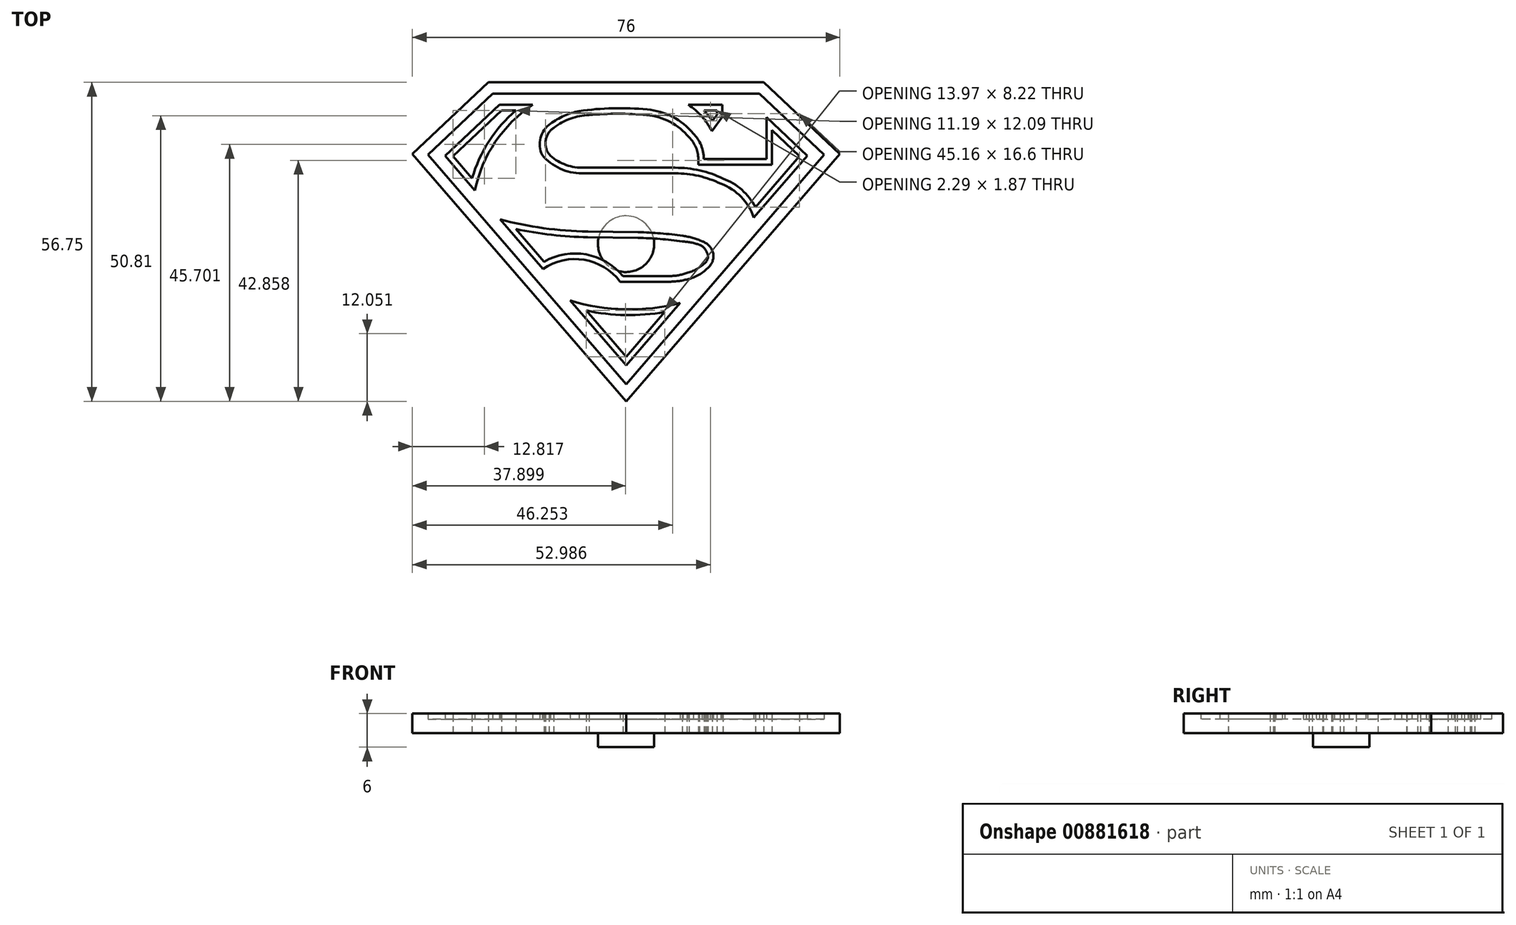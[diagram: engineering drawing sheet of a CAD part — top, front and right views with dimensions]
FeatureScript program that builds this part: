
annotation { "Feature Type Name" : "Feature", "Feature Type Description" : "" }
export const myFeature = defineFeature(function(context is Context, id is Id, definition is map)
    precondition{}
    {
        {
            var Q0;
            Q0=qCreatedBy(makeId("Top.planeOp"),FACE);
            var sketch = newSketch(context, id + "F0", { "sketchPlane" : qUnion([Q0])});
            skLineSegment(sketch, "E0", {"start": v(-24.5, 28.75) * mm, "end": v(24.5, 28.75) * mm});
            skLineSegment(sketch, "E1", {"start": v(24.5, 28.75) * mm, "end": v(38, 16) * mm});
            skLineSegment(sketch, "E2", {"start": v(38, 16) * mm, "end": v(0, -28) * mm});
            skLineSegment(sketch, "E3", {"start": v(0, -28) * mm, "end": v(-38, 16) * mm});
            skLineSegment(sketch, "E4", {"start": v(-38, 16) * mm, "end": v(-24.5, 28.75) * mm});
            skSolve(sketch);
        }
        {
            var Q0;
            Q0 = qSketchRegion(id + "F0", true);
            extrude(context, id + "F1", {"entities" : qUnion([Q0]), "depth" : 2.5 * mm, "offsetDistance" : 25 * mm});
        }
        {
            var Q0;
            Q0=makeQuery(id+"F1.opExtrude","CAP_FACE",FACE,{"disambiguationData":[OSD([sQuery(id+"F0.wireOp",EDGE,"E0"),sQuery(id+"F0.wireOp",EDGE,"E1"),sQuery(id+"F0.wireOp",EDGE,"E2"),sQuery(id+"F0.wireOp",EDGE,"E3"),sQuery(id+"F0.wireOp",EDGE,"E4")])],"isStart":false});
            var sketch = newSketch(context, id + "F2", { "sketchPlane" : qUnion([Q0])});
            skLineSegment(sketch, "E5", {"start": v(-38, 16) * mm, "end": v(-24.5, 28.75) * mm});
            skLineSegment(sketch, "E6", {"start": v(-24.5, 28.75) * mm, "end": v(24.5, 28.75) * mm});
            skLineSegment(sketch, "E7", {"start": v(24.5, 28.75) * mm, "end": v(38, 16) * mm});
            skLineSegment(sketch, "E8", {"start": v(38, 16) * mm, "end": v(0, -28) * mm});
            skLineSegment(sketch, "E9", {"start": v(0, -28) * mm, "end": v(-38, 16) * mm});
            skLineSegment(sketch, "E10.0", {"start": v(-35.24, 15.86) * mm, "end": v(0, -24.94) * mm});
            skLineSegment(sketch, "E10.1", {"start": v(-23.7, 26.75) * mm, "end": v(-35.24, 15.86) * mm});
            skLineSegment(sketch, "E10.2", {"start": v(0, -24.94) * mm, "end": v(35.24, 15.86) * mm});
            skLineSegment(sketch, "E10.3", {"start": v(35.24, 15.86) * mm, "end": v(23.7, 26.75) * mm});
            skLineSegment(sketch, "E10.4", {"start": v(23.7, 26.75) * mm, "end": v(-23.7, 26.75) * mm});
            skLineSegment(sketch, "E11", {"start": v(-32.16, 15.66) * mm, "end": v(-22.54, 24.75) * mm});
            skLineSegment(sketch, "E12", {"start": v(-22.54, 24.75) * mm, "end": v(-16.62, 24.75) * mm});
            skLineSegment(sketch, "E13", {"start": v(-32.16, 15.66) * mm, "end": v(-26.87, 9.54) * mm});
            skLineSegment(sketch, "E14", {"start": v(32.21, 15.7) * mm, "end": v(22.71, 4.7) * mm});
            skLineSegment(sketch, "E15", {"start": v(32.21, 15.7) * mm, "end": v(24.97, 22.54) * mm});
            skLineSegment(sketch, "E16", {"start": v(-22.39, 4.35) * mm, "end": v(-14.78, -4.46) * mm});
            skLineSegment(sketch, "E17", {"start": v(-9.95, -10.06) * mm, "end": v(0.01, -21.59) * mm});
            skLineSegment(sketch, "E18", {"start": v(9.6, -10.48) * mm, "end": v(0.01, -21.59) * mm});
            skLineSegment(sketch, "E19", {"start": v(11.1, 24.75) * mm, "end": v(17.13, 24.75) * mm});
            skArc(sketch, "E20", {"start": v(-16.62, 24.75) * mm, "mid": v(-23.24, 18.15) * mm, "end": v(-26.87, 9.54) * mm});
            skArc(sketch, "E21", {"start": v(15.26, 20.07) * mm, "mid": v(13.48, 22.67) * mm, "end": v(11.1, 24.75) * mm});
            skLineSegment(sketch, "E22", {"start": v(17.13, 24.75) * mm, "end": v(17.13, 22.58) * mm});
            skLineSegment(sketch, "E23", {"start": v(17.13, 22.58) * mm, "end": v(15.26, 20.07) * mm});
            skLineSegment(sketch, "E24", {"start": v(24.97, 22.54) * mm, "end": v(24.97, 15.1) * mm});
            skLineSegment(sketch, "E25", {"start": v(-7.86, 12.56) * mm, "end": v(8.75, 12.56) * mm});
            skArc(sketch, "E26", {"start": v(22.71, 4.7) * mm, "mid": v(20.46, 8.36) * mm, "end": v(16.86, 10.72) * mm});
            skArc(sketch, "E27", {"start": v(16.86, 10.72) * mm, "mid": v(12.9, 12.1) * mm, "end": v(8.75, 12.56) * mm});
            skLineSegment(sketch, "E28", {"start": v(-1.06, -6.7) * mm, "end": v(7.73, -6.7) * mm});
            skArc(sketch, "E29", {"start": v(-1.06, -6.7) * mm, "mid": v(-7.47, -2.82) * mm, "end": v(-14.78, -4.46) * mm});
            skArc(sketch, "E30", {"start": v(-22.39, 4.35) * mm, "mid": v(-14.66, 2.8) * mm, "end": v(-6.8, 2.21) * mm});
            skLineSegment(sketch, "E31", {"start": v(-6.8, 2.21) * mm, "end": v(2.13, 2.08) * mm});
            skArc(sketch, "E32", {"start": v(10.13, 1.43) * mm, "mid": v(6.14, 1.89) * mm, "end": v(2.13, 2.08) * mm});
            skArc(sketch, "E33", {"start": v(-9.95, -10.06) * mm, "mid": v(-0.2, -11.64) * mm, "end": v(9.6, -10.48) * mm});
            skLineSegment(sketch, "E34.0", {"start": v(-30.78, 15.6) * mm, "end": v(-22.14, 23.75) * mm});
            skLineSegment(sketch, "E35.0", {"start": v(-30.78, 15.6) * mm, "end": v(-27.38, 11.65) * mm});
            skLineSegment(sketch, "E36.0", {"start": v(-22.14, 23.75) * mm, "end": v(-19.6, 23.75) * mm});
            skArc(sketch, "E37.0", {"start": v(-19.6, 23.75) * mm, "mid": v(-24.37, 18.27) * mm, "end": v(-27.38, 11.65) * mm});
            skArc(sketch, "E38.0", {"start": v(15.36, 21.87) * mm, "mid": v(14.64, 22.84) * mm, "end": v(13.84, 23.75) * mm});
            skLineSegment(sketch, "E39.0", {"start": v(13.84, 23.75) * mm, "end": v(16.13, 23.75) * mm});
            skLineSegment(sketch, "E40.0", {"start": v(16.13, 23.75) * mm, "end": v(16.13, 22.9) * mm});
            skLineSegment(sketch, "E41.0", {"start": v(16.13, 22.9) * mm, "end": v(15.36, 21.87) * mm});
            skLineSegment(sketch, "E42.0", {"start": v(25.97, 20.22) * mm, "end": v(25.97, 14.1) * mm});
            skLineSegment(sketch, "E43.0", {"start": v(30.83, 15.63) * mm, "end": v(25.97, 20.22) * mm});
            skLineSegment(sketch, "E44.0", {"start": v(30.83, 15.63) * mm, "end": v(23, 6.56) * mm});
            skArc(sketch, "E45.0", {"start": v(23, 6.56) * mm, "mid": v(20.59, 9.62) * mm, "end": v(17.25, 11.64) * mm});
            skArc(sketch, "E46.0", {"start": v(17.25, 11.64) * mm, "mid": v(13.1, 13.07) * mm, "end": v(8.75, 13.56) * mm});
            skLineSegment(sketch, "E47.0", {"start": v(-7.86, 13.56) * mm, "end": v(8.75, 13.56) * mm});
            skLineSegment(sketch, "E48", {"start": v(25.97, 14.1) * mm, "end": v(12.83, 14.1) * mm});
            skLineSegment(sketch, "E49", {"start": v(24.97, 15.1) * mm, "end": v(13.83, 15.1) * mm});
            skPoint(sketch, "E50.orphan", {"position": v(25.97, 17.25) * mm});
            skLineSegment(sketch, "E51", {"start": v(12.83, 14.1) * mm, "end": v(12.83, 15.1) * mm});
            skArc(sketch, "E52", {"start": v(12.83, 15.1) * mm, "mid": v(12.41, 17.2) * mm, "end": v(11.21, 18.96) * mm});
            skArc(sketch, "E53", {"start": v(11.21, 18.96) * mm, "mid": v(7.84, 21.7) * mm, "end": v(3.67, 22.93) * mm});
            skArc(sketch, "E54.0", {"start": v(11.95, 19.63) * mm, "mid": v(8.28, 22.6) * mm, "end": v(3.75, 23.92) * mm});
            skArc(sketch, "E55.0", {"start": v(13.83, 15.1) * mm, "mid": v(13.34, 17.56) * mm, "end": v(11.95, 19.63) * mm});
            skArc(sketch, "E56", {"start": v(-13.7, 15.98) * mm, "mid": v(-11.03, 14.19) * mm, "end": v(-7.86, 13.56) * mm});
            skArc(sketch, "E57.0", {"start": v(-14.9, 15.8) * mm, "mid": v(-11.74, 13.4) * mm, "end": v(-7.86, 12.56) * mm});
            skArc(sketch, "E58", {"start": v(3.67, 22.93) * mm, "mid": v(-1.45, 23.16) * mm, "end": v(-6.56, 22.93) * mm});
            skArc(sketch, "E59", {"start": v(3.75, 23.92) * mm, "mid": v(-2.31, 24.13) * mm, "end": v(-8.35, 23.62) * mm});
            skArc(sketch, "E60", {"start": v(-6.56, 22.93) * mm, "mid": v(-9.9, 22.3) * mm, "end": v(-12.86, 20.66) * mm});
            skArc(sketch, "E61", {"start": v(-8.35, 23.62) * mm, "mid": v(-11.02, 22.78) * mm, "end": v(-13.44, 21.37) * mm});
            skArc(sketch, "E62", {"start": v(-12.86, 20.66) * mm, "mid": v(-14.27, 18.5) * mm, "end": v(-13.7, 15.98) * mm});
            skArc(sketch, "E63", {"start": v(-13.44, 21.37) * mm, "mid": v(-15.21, 18.85) * mm, "end": v(-14.9, 15.8) * mm});
            skArc(sketch, "E64.0", {"start": v(-7.09, -11.84) * mm, "mid": v(-0.11, -12.64) * mm, "end": v(6.89, -12.1) * mm});
            skLineSegment(sketch, "E65.0", {"start": v(6.89, -12.1) * mm, "end": v(0.01, -20.06) * mm});
            skLineSegment(sketch, "E66.0", {"start": v(-7.09, -11.84) * mm, "end": v(0.01, -20.06) * mm});
            skLineSegment(sketch, "E67.0", {"start": v(-19.6, 2.66) * mm, "end": v(-14.58, -3.16) * mm});
            skLineSegment(sketch, "E68.0", {"start": v(-0.57, -5.7) * mm, "end": v(7.73, -5.7) * mm});
            skLineSegment(sketch, "E69.0", {"start": v(-6.8, 1.21) * mm, "end": v(2.12, 1.08) * mm});
            skArc(sketch, "E70.0", {"start": v(-0.57, -5.7) * mm, "mid": v(-7.11, -1.87) * mm, "end": v(-14.58, -3.16) * mm});
            skArc(sketch, "E71.0", {"start": v(-19.6, 2.66) * mm, "mid": v(-13.24, 1.62) * mm, "end": v(-6.8, 1.21) * mm});
            skArc(sketch, "E72.0", {"start": v(9.98, 0.44) * mm, "mid": v(6.06, 0.9) * mm, "end": v(2.12, 1.08) * mm});
            skArc(sketch, "E73", {"start": v(7.73, -6.7) * mm, "mid": v(9.46, -6.59) * mm, "end": v(11.16, -6.22) * mm});
            skArc(sketch, "E74", {"start": v(7.73, -5.7) * mm, "mid": v(9.3, -5.57) * mm, "end": v(10.8, -5.16) * mm});
            skArc(sketch, "E75", {"start": v(11.16, -6.22) * mm, "mid": v(13.23, -5.33) * mm, "end": v(14.93, -3.86) * mm});
            skArc(sketch, "E76", {"start": v(10.8, -5.16) * mm, "mid": v(12.57, -4.46) * mm, "end": v(14.1, -3.33) * mm});
            skArc(sketch, "E77", {"start": v(14.93, -3.86) * mm, "mid": v(15.5, -2.6) * mm, "end": v(15.35, -1.2) * mm});
            skArc(sketch, "E78", {"start": v(14.1, -3.33) * mm, "mid": v(14.56, -2.47) * mm, "end": v(14.37, -1.52) * mm});
            skArc(sketch, "E79", {"start": v(15.35, -1.2) * mm, "mid": v(14.6, -0.17) * mm, "end": v(13.5, 0.47) * mm});
            skArc(sketch, "E80", {"start": v(14.37, -1.52) * mm, "mid": v(13.86, -0.7) * mm, "end": v(13.07, -0.17) * mm});
            skPoint(sketch, "E80.endSnap0", {"position": v(14.6, -0.17) * mm});
            skArc(sketch, "E81", {"start": v(13.5, 0.47) * mm, "mid": v(11.85, 1.08) * mm, "end": v(10.13, 1.43) * mm});
            skArc(sketch, "E82", {"start": v(13.07, -0.17) * mm, "mid": v(11.55, 0.26) * mm, "end": v(9.98, 0.44) * mm});
            skPoint(sketch, "E83.orphan", {"position": v(-6.72, 23.83) * mm});
            skPoint(sketch, "E84.orphan", {"position": v(13.97, 15.1) * mm});
            skSolve(sketch);
        }
        {
            var Q0;
            Q0=makeQuery(id+"F2.imprint","IMPRINT",FACE,{"disambiguationData":[TD([[makeQuery(id+"F2.imprint","IMPRINT",EDGE,{"derivedFrom":sQuery(id+"F2.wireOp",EDGE,"E11")}),-1.0]])]});
            var Q1;
            Q1=makeQuery(id+"F2.imprint","IMPRINT",FACE,{"disambiguationData":[TD([[makeQuery(id+"F2.imprint","IMPRINT",EDGE,{"derivedFrom":sQuery(id+"F2.wireOp",EDGE,"E16")}),1.0]])]});
            var Q2;
            Q2=makeQuery(id+"F2.imprint","IMPRINT",FACE,{"disambiguationData":[TD([[makeQuery(id+"F2.imprint","IMPRINT",EDGE,{"derivedFrom":sQuery(id+"F2.wireOp",EDGE,"E19")}),-1.0]])]});
            var Q3;
            Q3=makeQuery(id+"F2.imprint","IMPRINT",FACE,{"disambiguationData":[TD([[makeQuery(id+"F2.imprint","IMPRINT",EDGE,{"derivedFrom":sQuery(id+"F2.wireOp",EDGE,"E5")}),-1.0]])]});
            var Q4;
            Q4=makeQuery(id+"F2.imprint","IMPRINT",FACE,{"disambiguationData":[TD([[makeQuery(id+"F2.imprint","IMPRINT",EDGE,{"derivedFrom":sQuery(id+"F2.wireOp",EDGE,"E17")}),1.0]])]});
            var Q5;
            Q5=makeQuery(id+"F2.imprint","IMPRINT",FACE,{"disambiguationData":[TD([[makeQuery(id+"F2.imprint","IMPRINT",EDGE,{"derivedFrom":sQuery(id+"F2.wireOp",EDGE,"E14")}),-1.0]])]});
            extrude(context, id + "F3", {"entities" : qUnion([Q0, Q1, Q2, Q3, Q4, Q5]), "operationType" : NewBodyOperationType.ADD, "depth" : 1 * mm, "offsetDistance" : 25 * mm});
        }
        {
            var Q0;
            Q0=makeQuery(id+"F3.boolean.opBoolean","SPLIT",FACE,{"disambiguationData":[TD([makeQuery(id+"F3.opExtrude","SWEPT_FACE",FACE,{"disambiguationData":[OSD([sQuery(id+"F2.wireOp",EDGE,"E42.0")])]})])],"derivedFrom":makeQuery(id+"F1.opExtrude","CAP_FACE",FACE,{"disambiguationData":[OSD([sQuery(id+"F0.wireOp",EDGE,"E0"),sQuery(id+"F0.wireOp",EDGE,"E1"),sQuery(id+"F0.wireOp",EDGE,"E2"),sQuery(id+"F0.wireOp",EDGE,"E3"),sQuery(id+"F0.wireOp",EDGE,"E4")])],"isStart":false})});
            var Q1;
            Q1=makeQuery(id+"F3.boolean.opBoolean","SPLIT",FACE,{"disambiguationData":[TD([makeQuery(id+"F3.opExtrude","SWEPT_FACE",FACE,{"disambiguationData":[OSD([sQuery(id+"F2.wireOp",EDGE,"E38.0")])]})])],"derivedFrom":makeQuery(id+"F1.opExtrude","CAP_FACE",FACE,{"disambiguationData":[OSD([sQuery(id+"F0.wireOp",EDGE,"E0"),sQuery(id+"F0.wireOp",EDGE,"E1"),sQuery(id+"F0.wireOp",EDGE,"E2"),sQuery(id+"F0.wireOp",EDGE,"E3"),sQuery(id+"F0.wireOp",EDGE,"E4")])],"isStart":false})});
            var Q2;
            Q2=makeQuery(id+"F3.boolean.opBoolean","SPLIT",FACE,{"disambiguationData":[TD([makeQuery(id+"F3.opExtrude","SWEPT_FACE",FACE,{"disambiguationData":[OSD([sQuery(id+"F2.wireOp",EDGE,"E34.0")])]})])],"derivedFrom":makeQuery(id+"F1.opExtrude","CAP_FACE",FACE,{"disambiguationData":[OSD([sQuery(id+"F0.wireOp",EDGE,"E0"),sQuery(id+"F0.wireOp",EDGE,"E1"),sQuery(id+"F0.wireOp",EDGE,"E2"),sQuery(id+"F0.wireOp",EDGE,"E3"),sQuery(id+"F0.wireOp",EDGE,"E4")])],"isStart":false})});
            var Q3;
            Q3=makeQuery(id+"F3.boolean.opBoolean","SPLIT",FACE,{"disambiguationData":[TD([makeQuery(id+"F3.opExtrude","SWEPT_FACE",FACE,{"disambiguationData":[OSD([sQuery(id+"F2.wireOp",EDGE,"E67.0")])]})])],"derivedFrom":makeQuery(id+"F1.opExtrude","CAP_FACE",FACE,{"disambiguationData":[OSD([sQuery(id+"F0.wireOp",EDGE,"E0"),sQuery(id+"F0.wireOp",EDGE,"E1"),sQuery(id+"F0.wireOp",EDGE,"E2"),sQuery(id+"F0.wireOp",EDGE,"E3"),sQuery(id+"F0.wireOp",EDGE,"E4")])],"isStart":false})});
            var Q4;
            Q4=makeQuery(id+"F3.boolean.opBoolean","SPLIT",FACE,{"disambiguationData":[TD([makeQuery(id+"F3.opExtrude","SWEPT_FACE",FACE,{"disambiguationData":[OSD([sQuery(id+"F2.wireOp",EDGE,"E64.0")])]})])],"derivedFrom":makeQuery(id+"F1.opExtrude","CAP_FACE",FACE,{"disambiguationData":[OSD([sQuery(id+"F0.wireOp",EDGE,"E0"),sQuery(id+"F0.wireOp",EDGE,"E1"),sQuery(id+"F0.wireOp",EDGE,"E2"),sQuery(id+"F0.wireOp",EDGE,"E3"),sQuery(id+"F0.wireOp",EDGE,"E4")])],"isStart":false})});
            extrude(context, id + "F4", {"entities" : qUnion([Q0, Q1, Q2, Q3, Q4]), "operationType" : NewBodyOperationType.REMOVE, "oppositeDirection" : true, "depth" : 2.5 * mm, "offsetDistance" : 25 * mm});
        }
        {
            var Q0;
            Q0=qCreatedBy(makeId("Top.planeOp"),FACE);
            var sketch = newSketch(context, id + "F5", { "sketchPlane" : qUnion([Q0])});
            skCircle(sketch, "E85", {"center": v(0, 0) * mm, "radius": 5 * mm});
            skSolve(sketch);
        }
        {
            var Q0;
            Q0 = qSketchRegion(id + "F5", true);
            extrude(context, id + "F6", {"entities" : qUnion([Q0]), "operationType" : NewBodyOperationType.ADD, "oppositeDirection" : true, "depth" : 2.5 * mm, "offsetDistance" : 25 * mm});
        }
    });
